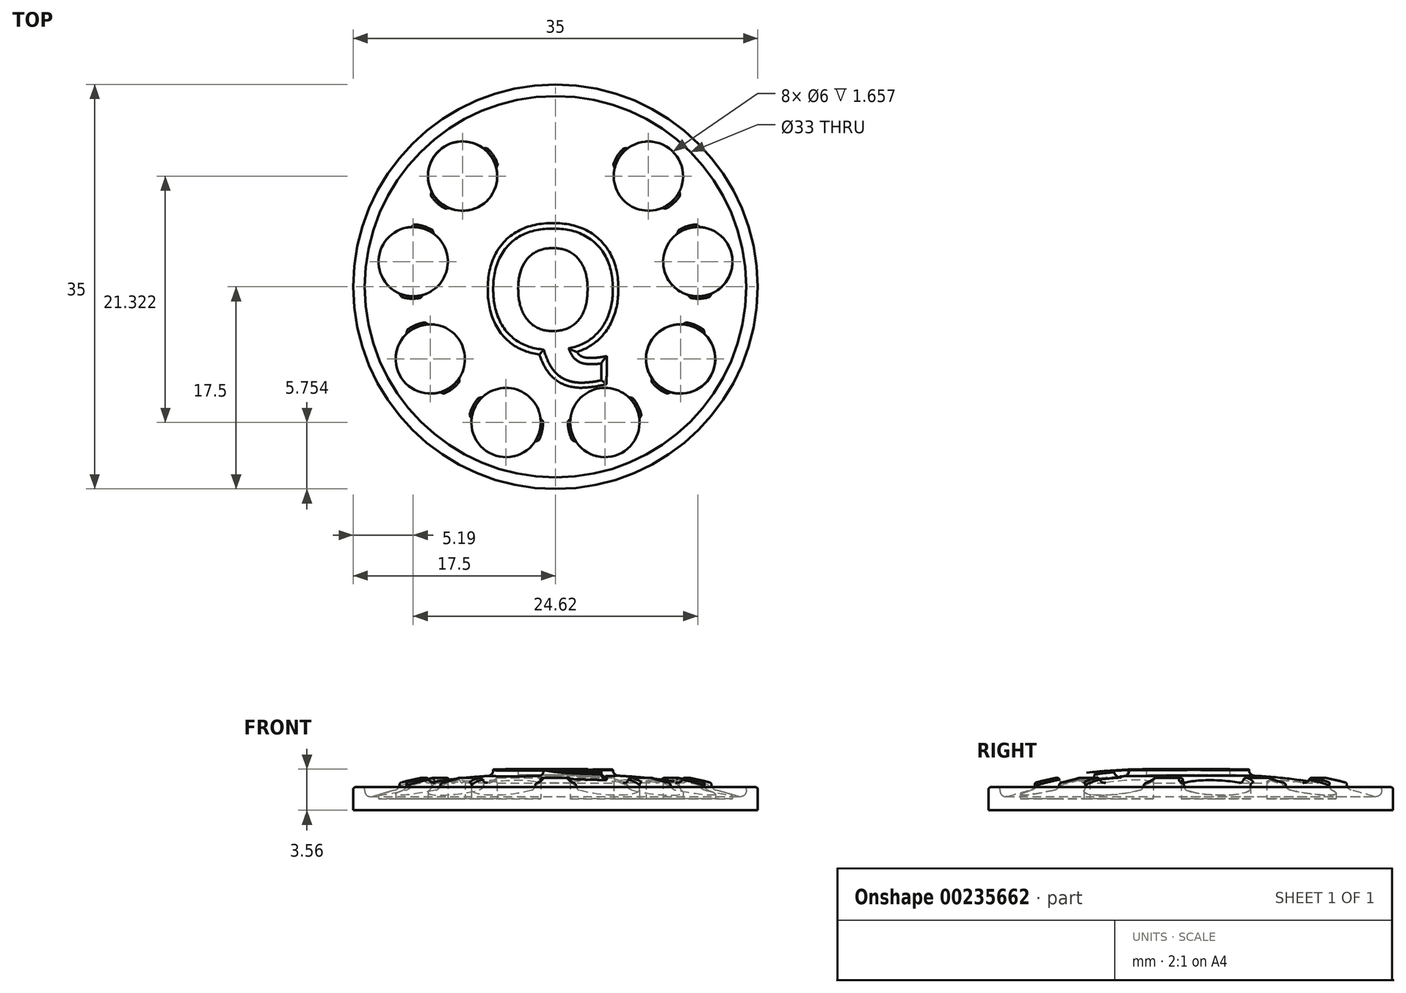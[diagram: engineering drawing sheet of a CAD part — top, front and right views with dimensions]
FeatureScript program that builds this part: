
annotation { "Feature Type Name" : "Feature", "Feature Type Description" : "" }
export const myFeature = defineFeature(function(context is Context, id is Id, definition is map)
    precondition{}
    {
        {
            var Q0;
            Q0=qCreatedBy(makeId("Top.planeOp"),FACE);
            var sketch = newSketch(context, id + "F0", { "sketchPlane" : qUnion([Q0])});
            skCircle(sketch, "E0", {"center": v(0, 0) * mm, "radius": 17.5 * mm});
            skCircle(sketch, "E1", {"center": v(0, 0) * mm, "radius": 16.5 * mm});
            skLineSegment(sketch, "E2", {"start": v(0, 0) * mm, "end": v(0, 16.5) * mm, "construction": true});
            skLineSegment(sketch, "E3", {"start": v(0, 0) * mm, "end": v(0, -16.5) * mm, "construction": true});
            skText(sketch, "E4", { "text": "Q", "fontName": "Arimo-Bold.ttf"});
            skCircle(sketch, "E5", {"center": v(0, 0) * mm, "radius": 12.5 * mm, "construction": true});
            skCircle(sketch, "E6", {"center": v(0, 12.5) * mm, "radius": 3 * mm});
            skCircle(sketch, "E7.1.0", {"center": v(-8.03, 9.58) * mm, "radius": 3 * mm});
            skCircle(sketch, "E7.2.0", {"center": v(-12.31, 2.17) * mm, "radius": 3 * mm});
            skCircle(sketch, "E7.3.0", {"center": v(-10.83, -6.25) * mm, "radius": 3 * mm});
            skCircle(sketch, "E7.4.0", {"center": v(-4.28, -11.75) * mm, "radius": 3 * mm});
            skCircle(sketch, "E7.5.0", {"center": v(4.28, -11.75) * mm, "radius": 3 * mm});
            skCircle(sketch, "E7.6.0", {"center": v(10.83, -6.25) * mm, "radius": 3 * mm});
            skCircle(sketch, "E7.7.0", {"center": v(12.31, 2.17) * mm, "radius": 3 * mm});
            skCircle(sketch, "E8.1.8.0", {"center": v(8.03, 9.58) * mm, "radius": 3 * mm});
            const initialGuessF0  = {"E4": [-0.006, -0.00537, 1, 0, 0.01073]};
            skSetInitialGuess(sketch, initialGuessF0);
            skSolve(sketch);
        }
        {
            var Q0;
            Q0=qCreatedBy(makeId("Front.planeOp"),FACE);
            var sketch = newSketch(context, id + "F1", { "sketchPlane" : qUnion([Q0])});
            skLineSegment(sketch, "E9.0", {"start": v(-16.5, 0) * mm, "end": v(16.5, 0) * mm});
            skLineSegment(sketch, "E10.0", {"start": v(-17.5, 0) * mm, "end": v(17.5, 0) * mm});
            skLineSegment(sketch, "E11", {"start": v(-17.5, 0) * mm, "end": v(-17.5, 1.8) * mm});
            skLineSegment(sketch, "E12", {"start": v(-17.3, 2) * mm, "end": v(-16.7, 2) * mm});
            skLineSegment(sketch, "E13", {"start": v(-16.5, 1.8) * mm, "end": v(-16.5, 1.67) * mm});
            skLineSegment(sketch, "E14", {"start": v(0, 0) * mm, "end": v(0, 3) * mm});
            skFitSpline(sketch, "E15", {"points": [v(-16.5, 1) * mm, v(0, 3) * mm], "startDerivative": vector(10.42, 3.22) * mm, "endDerivative": vector(24.57, -1.03) * mm});
            skArc(sketch, "E16.filletArc", {"start": v(-16.5, 1.67) * mm, "mid": v(-16.3, 1.27) * mm, "end": v(-15.86, 1.2) * mm});
            skPoint(sketch, "E17.visualSharp", {"position": v(-17.5, 2) * mm});
            skArc(sketch, "E17.filletArc", {"start": v(-17.3, 2) * mm, "mid": v(-17.44, 1.94) * mm, "end": v(-17.5, 1.8) * mm});
            skPoint(sketch, "E18.visualSharp", {"position": v(-16.5, 2) * mm});
            skArc(sketch, "E18.filletArc", {"start": v(-16.5, 1.8) * mm, "mid": v(-16.56, 1.94) * mm, "end": v(-16.7, 2) * mm});
            skLineSegment(sketch, "E19", {"start": v(-15.86, 1.2) * mm, "end": v(-15.86, 2.88) * mm, "construction": true});
            skLineSegment(sketch, "E20", {"start": v(0, 3) * mm, "end": v(0, 5.02) * mm, "construction": true});
            skPoint(sketch, "E21", {"position": v(0, 3.5) * mm});
            skPoint(sketch, "E22", {"position": v(-15.86, 1.7) * mm});
            skFitSpline(sketch, "E23", {"points": [v(-15.86, 1.7) * mm, v(0, 3.5) * mm], "startDerivative": vector(11.8, 3.63) * mm, "endDerivative": vector(24.86, -0.94) * mm});
            skLineSegment(sketch, "E24", {"start": v(-15.86, 1.7) * mm, "end": v(-15.86, 7.13) * mm});
            skPoint(sketch, "E24.endSnap0", {"position": v(-15.86, 2.04) * mm});
            skLineSegment(sketch, "E25", {"start": v(0, 3.5) * mm, "end": v(0, 7.13) * mm});
            skLineSegment(sketch, "E26", {"start": v(0, 7.13) * mm, "end": v(-15.86, 7.13) * mm});
            skSolve(sketch);
        }
        {
            var Q0;
            Q0=qCreatedBy(makeId("Top.planeOp"),FACE);
            cPlane(context, id + "F2", {"entities" : qUnion([Q0]), "cplaneType" : CPlaneType.OFFSET, "offset" : 1 * mm, "width" : 150 * mm, "height" : 150 * mm});
        }
        {
            var Q0;
            Q0=qCreatedBy(id+"F2.planeOp",FACE);
            var sketch = newSketch(context, id + "F3", { "sketchPlane" : qUnion([Q0])});
            skCircle(sketch, "E27.1", {"center": v(12.31, 2.17) * mm, "radius": 3 * mm});
            skCircle(sketch, "E27.2", {"center": v(10.83, -6.25) * mm, "radius": 3 * mm});
            skCircle(sketch, "E27.3", {"center": v(4.28, -11.75) * mm, "radius": 3 * mm});
            skCircle(sketch, "E27.4", {"center": v(-4.28, -11.75) * mm, "radius": 3 * mm});
            skCircle(sketch, "E27.5", {"center": v(-10.83, -6.25) * mm, "radius": 3 * mm});
            skCircle(sketch, "E27.6", {"center": v(-12.31, 2.17) * mm, "radius": 3 * mm});
            skCircle(sketch, "E27.7", {"center": v(-8.03, 9.58) * mm, "radius": 3 * mm});
            skCircle(sketch, "E28.0", {"center": v(8.03, 9.58) * mm, "radius": 3 * mm});
            skCircle(sketch, "E29.0", {"center": v(0, 0) * mm, "radius": 12.5 * mm, "construction": true});
            skArc(sketch, "E30", {"start": v(-10.71, 8.22) * mm, "mid": v(-11.7, 6.75) * mm, "end": v(-12.47, 5.17) * mm});
            skArc(sketch, "E31", {"start": v(-9.25, 6.83) * mm, "mid": v(-9.96, 5.75) * mm, "end": v(-10.54, 4.6) * mm});
            skArc(sketch, "E32.0", {"start": v(-2.92, 13.18) * mm, "mid": v(-2.98, 12.16) * mm, "end": v(-2.7, 11.18) * mm});
            skArc(sketch, "E33.trimOffspring", {"start": v(-13.49, -0.59) * mm, "mid": v(-13.3, -2.34) * mm, "end": v(-12.88, -4.06) * mm});
            skArc(sketch, "E34.trimOffspring", {"start": v(-11.48, -0.71) * mm, "mid": v(-11.33, -2) * mm, "end": v(-11.03, -3.26) * mm});
            skArc(sketch, "E35.trimOffspring", {"start": v(-9.95, -9.12) * mm, "mid": v(-8.68, -10.34) * mm, "end": v(-7.25, -11.39) * mm});
            skArc(sketch, "E36.trimOffspring", {"start": v(-8.34, -7.92) * mm, "mid": v(-7.4, -8.8) * mm, "end": v(-6.36, -9.58) * mm});
            skArc(sketch, "E37.trimOffspring", {"start": v(-1.3, -11.43) * mm, "mid": v(0, -11.5) * mm, "end": v(1.3, -11.43) * mm});
            skArc(sketch, "E38.trimOffspring", {"start": v(-1.76, -13.38) * mm, "mid": v(0, -13.5) * mm, "end": v(1.76, -13.38) * mm});
            skArc(sketch, "E39.trimOffspring", {"start": v(6.36, -9.58) * mm, "mid": v(7.4, -8.8) * mm, "end": v(8.34, -7.92) * mm});
            skArc(sketch, "E40.trimOffspring", {"start": v(7.25, -11.39) * mm, "mid": v(8.68, -10.34) * mm, "end": v(9.95, -9.12) * mm});
            skArc(sketch, "E41.trimOffspring", {"start": v(11.03, -3.26) * mm, "mid": v(11.33, -2) * mm, "end": v(11.48, -0.71) * mm});
            skArc(sketch, "E42.trimOffspring", {"start": v(12.88, -4.06) * mm, "mid": v(13.3, -2.34) * mm, "end": v(13.49, -0.59) * mm});
            skArc(sketch, "E43.trimOffspring", {"start": v(10.54, 4.6) * mm, "mid": v(9.96, 5.75) * mm, "end": v(9.25, 6.83) * mm});
            skArc(sketch, "E44.trimOffspring", {"start": v(12.47, 5.17) * mm, "mid": v(11.7, 6.75) * mm, "end": v(10.71, 8.22) * mm});
            skArc(sketch, "E45.trimOffspring", {"start": v(5.12, 10.3) * mm, "mid": v(0, 11.5) * mm, "end": v(-5.12, 10.3) * mm});
            skArc(sketch, "E46.trimOffspring", {"start": v(6.23, 11.97) * mm, "mid": v(0, 13.5) * mm, "end": v(-6.23, 11.97) * mm});
            skArc(sketch, "E47.trimOffspring", {"start": v(2.7, 11.18) * mm, "mid": v(2.98, 12.16) * mm, "end": v(2.92, 13.18) * mm});
            skSolve(sketch);
        }
        {
            var Q0;
            {var subQ0=sQuery(id+"F1.wireOp",EDGE,"E11");Q0=makeQuery(id+"F1.imprint","IMPRINT",FACE,{"disambiguationData":[TD([[makeQuery(id+"F1.imprint","IMPRINT",EDGE,{"derivedFrom":subQ0}),-1.0]])]});}
            var Q1;
            Q1=sQuery(id+"F1.wireOp",EDGE,"E14");
            revolve(context, id + "F4", {"entities" : qUnion([Q0]), "axis" : qUnion([Q1]), "revolveType" : RevolveType.FULL});
        }
        {
            var Q0;
            {var subQ0=sQuery(id+"F3.wireOp",EDGE,"E30");Q0=makeQuery(id+"F3.imprint","IMPRINT",FACE,{"disambiguationData":[TD([[makeQuery(id+"F3.imprint","IMPRINT",EDGE,{"derivedFrom":subQ0}),1.0]])]});}
            var Q1;
            {var subQ0=sQuery(id+"F3.wireOp",EDGE,"E33.trimOffspring");Q1=makeQuery(id+"F3.imprint","IMPRINT",FACE,{"disambiguationData":[TD([[makeQuery(id+"F3.imprint","IMPRINT",EDGE,{"derivedFrom":subQ0}),1.0]])]});}
            var Q2;
            {var subQ0=sQuery(id+"F3.wireOp",EDGE,"E35.trimOffspring");Q2=makeQuery(id+"F3.imprint","IMPRINT",FACE,{"disambiguationData":[TD([[makeQuery(id+"F3.imprint","IMPRINT",EDGE,{"derivedFrom":subQ0}),1.0]])]});}
            var Q3;
            {var subQ0=sQuery(id+"F3.wireOp",EDGE,"E37.trimOffspring");Q3=makeQuery(id+"F3.imprint","IMPRINT",FACE,{"disambiguationData":[TD([[makeQuery(id+"F3.imprint","IMPRINT",EDGE,{"derivedFrom":subQ0}),-1.0]])]});}
            var Q4;
            {var subQ0=sQuery(id+"F3.wireOp",EDGE,"E39.trimOffspring");Q4=makeQuery(id+"F3.imprint","IMPRINT",FACE,{"disambiguationData":[TD([[makeQuery(id+"F3.imprint","IMPRINT",EDGE,{"derivedFrom":subQ0}),-1.0]])]});}
            var Q5;
            {var subQ0=sQuery(id+"F3.wireOp",EDGE,"E41.trimOffspring");Q5=makeQuery(id+"F3.imprint","IMPRINT",FACE,{"disambiguationData":[TD([[makeQuery(id+"F3.imprint","IMPRINT",EDGE,{"derivedFrom":subQ0}),-1.0]])]});}
            var Q6;
            {var subQ0=sQuery(id+"F3.wireOp",EDGE,"E43.trimOffspring");Q6=makeQuery(id+"F3.imprint","IMPRINT",FACE,{"disambiguationData":[TD([[makeQuery(id+"F3.imprint","IMPRINT",EDGE,{"derivedFrom":subQ0}),-1.0]])]});}
            var Q7;
            {var subQ5=sQuery(id+"F3.wireOp",EDGE,"E47.trimOffspring");Q7=makeQuery(id+"F3.imprint","IMPRINT",FACE,{"disambiguationData":[TD([[makeQuery(id+"F3.imprint","IMPRINT",EDGE,{"derivedFrom":subQ5}),-1.0]])]});}
            var Q8;
            {var subQ0=sQuery(id+"F3.wireOp",EDGE,"E32.0");Q8=makeQuery(id+"F3.imprint","IMPRINT",FACE,{"disambiguationData":[TD([[makeQuery(id+"F3.imprint","IMPRINT",EDGE,{"derivedFrom":subQ0}),1.0]])]});}
            var Q9;
            {var subQ5=sQuery(id+"F3.wireOp",EDGE,"E32.0");Q9=makeQuery(id+"F3.imprint","IMPRINT",FACE,{"disambiguationData":[TD([[makeQuery(id+"F3.imprint","IMPRINT",EDGE,{"derivedFrom":subQ5}),-1.0]])]});}
            extrude(context, id + "F5", {"entities" : qUnion([Q0, Q1, Q2, Q3, Q4, Q5, Q6, Q7, Q8, Q9]), "operationType" : NewBodyOperationType.ADD, "depth" : 5 * mm});
        }
        {
            var Q0;
            Q0=makeQuery(id+"F0.imprint","IMPRINT",FACE,{"disambiguationData":[TD([[makeQuery(id+"F0.imprint","IMPRINT",EDGE,{"derivedFrom":sQuery(id+"F0.wireOp",EDGE,"E4.sketch_text.stroke-0")}),-1.0]])]});
            extrude(context, id + "F6", {"entities" : qUnion([Q0]), "operationType" : NewBodyOperationType.ADD, "depth" : 5 * mm});
        }
        {
            var Q0;
            Q0=makeQuery(id+"F1.imprint","IMPRINT",FACE,{"disambiguationData":[TD([[makeQuery(id+"F1.imprint","IMPRINT",EDGE,{"derivedFrom":sQuery(id+"F1.wireOp",EDGE,"E23")}),1.0]])]});
            var Q1;
            Q1=sQuery(id+"F1.wireOp",EDGE,"E25");
            revolve(context, id + "F7", {"operationType" : NewBodyOperationType.REMOVE, "entities" : qUnion([Q0]), "axis" : qUnion([Q1]), "revolveType" : RevolveType.FULL, "oppositeDirection" : true});
        }
        {
            var Q0;
            Q0=makeQuery(id+"F3.imprint","IMPRINT",FACE,{"disambiguationData":[TD([[makeQuery(id+"F3.imprint","IMPRINT",EDGE,{"derivedFrom":sQuery(id+"F3.wireOp",EDGE,"E27.7")}),1.0]])]});
            var Q1;
            Q1=makeQuery(id+"F3.imprint","IMPRINT",FACE,{"disambiguationData":[TD([[makeQuery(id+"F3.imprint","IMPRINT",EDGE,{"derivedFrom":sQuery(id+"F3.wireOp",EDGE,"E27.6")}),1.0]])]});
            var Q2;
            Q2=makeQuery(id+"F3.imprint","IMPRINT",FACE,{"disambiguationData":[TD([[makeQuery(id+"F3.imprint","IMPRINT",EDGE,{"derivedFrom":sQuery(id+"F3.wireOp",EDGE,"E27.5")}),1.0]])]});
            var Q3;
            Q3=makeQuery(id+"F3.imprint","IMPRINT",FACE,{"disambiguationData":[TD([[makeQuery(id+"F3.imprint","IMPRINT",EDGE,{"derivedFrom":sQuery(id+"F3.wireOp",EDGE,"E27.4")}),1.0]])]});
            var Q4;
            Q4=makeQuery(id+"F3.imprint","IMPRINT",FACE,{"disambiguationData":[TD([[makeQuery(id+"F3.imprint","IMPRINT",EDGE,{"derivedFrom":sQuery(id+"F3.wireOp",EDGE,"E27.3")}),1.0]])]});
            var Q5;
            Q5=makeQuery(id+"F3.imprint","IMPRINT",FACE,{"disambiguationData":[TD([[makeQuery(id+"F3.imprint","IMPRINT",EDGE,{"derivedFrom":sQuery(id+"F3.wireOp",EDGE,"E27.2")}),1.0]])]});
            var Q6;
            Q6=makeQuery(id+"F3.imprint","IMPRINT",FACE,{"disambiguationData":[TD([[makeQuery(id+"F3.imprint","IMPRINT",EDGE,{"derivedFrom":sQuery(id+"F3.wireOp",EDGE,"E27.1")}),1.0]])]});
            var Q7;
            Q7=makeQuery(id+"F3.imprint","IMPRINT",FACE,{"disambiguationData":[TD([[makeQuery(id+"F3.imprint","IMPRINT",EDGE,{"derivedFrom":sQuery(id+"F3.wireOp",EDGE,"E28.0")}),1.0]])]});
            extrude(context, id + "F8", {"entities" : qUnion([Q0, Q1, Q2, Q3, Q4, Q5, Q6, Q7]), "operationType" : NewBodyOperationType.REMOVE, "depth" : 25 * mm});
        }
        {
            var Q0;
            Q0=makeQuery(id+"F5.boolean.opBoolean","INTERSECT",EDGE,{"derivedFrom":[makeQuery(id+"F4.opRevolve","SWEPT_FACE",FACE,{"disambiguationData":[OSD([sQuery(id+"F1.wireOp",EDGE,"E15")])]}),makeQuery(id+"F5.opExtrude","SWEPT_FACE",FACE,{"disambiguationData":[OSD([sQuery(id+"F3.wireOp",EDGE,"E31")])]})]});
            var Q1;
            Q1=makeQuery(id+"F5.boolean.opBoolean","INTERSECT",EDGE,{"derivedFrom":[makeQuery(id+"F4.opRevolve","SWEPT_FACE",FACE,{"disambiguationData":[OSD([sQuery(id+"F1.wireOp",EDGE,"E15")])]}),makeQuery(id+"F5.opExtrude","SWEPT_FACE",FACE,{"disambiguationData":[OSD([sQuery(id+"F3.wireOp",EDGE,"E45.trimOffspring")])]})]});
            var Q2;
            Q2=makeQuery(id+"F5.boolean.opBoolean","INTERSECT",EDGE,{"derivedFrom":[makeQuery(id+"F4.opRevolve","SWEPT_FACE",FACE,{"disambiguationData":[OSD([sQuery(id+"F1.wireOp",EDGE,"E15")])]}),makeQuery(id+"F5.opExtrude","SWEPT_FACE",FACE,{"disambiguationData":[OSD([sQuery(id+"F3.wireOp",EDGE,"E43.trimOffspring")])]})]});
            var Q3;
            Q3=makeQuery(id+"F5.boolean.opBoolean","INTERSECT",EDGE,{"derivedFrom":[makeQuery(id+"F4.opRevolve","SWEPT_FACE",FACE,{"disambiguationData":[OSD([sQuery(id+"F1.wireOp",EDGE,"E15")])]}),makeQuery(id+"F5.opExtrude","SWEPT_FACE",FACE,{"disambiguationData":[OSD([sQuery(id+"F3.wireOp",EDGE,"E41.trimOffspring")])]})]});
            var Q4;
            Q4=makeQuery(id+"F5.boolean.opBoolean","INTERSECT",EDGE,{"derivedFrom":[makeQuery(id+"F4.opRevolve","SWEPT_FACE",FACE,{"disambiguationData":[OSD([sQuery(id+"F1.wireOp",EDGE,"E15")])]}),makeQuery(id+"F5.opExtrude","SWEPT_FACE",FACE,{"disambiguationData":[OSD([sQuery(id+"F3.wireOp",EDGE,"E39.trimOffspring")])]})]});
            var Q5;
            Q5=makeQuery(id+"F5.boolean.opBoolean","INTERSECT",EDGE,{"derivedFrom":[makeQuery(id+"F4.opRevolve","SWEPT_FACE",FACE,{"disambiguationData":[OSD([sQuery(id+"F1.wireOp",EDGE,"E15")])]}),makeQuery(id+"F5.opExtrude","SWEPT_FACE",FACE,{"disambiguationData":[OSD([sQuery(id+"F3.wireOp",EDGE,"E34.trimOffspring")])]})]});
            var Q6;
            Q6=makeQuery(id+"F5.boolean.opBoolean","INTERSECT",EDGE,{"derivedFrom":[makeQuery(id+"F4.opRevolve","SWEPT_FACE",FACE,{"disambiguationData":[OSD([sQuery(id+"F1.wireOp",EDGE,"E15")])]}),makeQuery(id+"F5.opExtrude","SWEPT_FACE",FACE,{"disambiguationData":[OSD([sQuery(id+"F3.wireOp",EDGE,"E36.trimOffspring")])]})]});
            var Q7;
            Q7=makeQuery(id+"F5.boolean.opBoolean","INTERSECT",EDGE,{"derivedFrom":[makeQuery(id+"F4.opRevolve","SWEPT_FACE",FACE,{"disambiguationData":[OSD([sQuery(id+"F1.wireOp",EDGE,"E15")])]}),makeQuery(id+"F5.opExtrude","SWEPT_FACE",FACE,{"disambiguationData":[OSD([sQuery(id+"F3.wireOp",EDGE,"E37.trimOffspring")])]})]});
            var Q8;
            Q8=makeQuery(id+"F5.boolean.opBoolean","INTERSECT",EDGE,{"derivedFrom":[makeQuery(id+"F4.opRevolve","SWEPT_FACE",FACE,{"disambiguationData":[OSD([sQuery(id+"F1.wireOp",EDGE,"E15")])]}),makeQuery(id+"F5.opExtrude","SWEPT_FACE",FACE,{"disambiguationData":[OSD([sQuery(id+"F3.wireOp",EDGE,"E38.trimOffspring")])]})]});
            var Q9;
            Q9=makeQuery(id+"F5.boolean.opBoolean","INTERSECT",EDGE,{"derivedFrom":[makeQuery(id+"F4.opRevolve","SWEPT_FACE",FACE,{"disambiguationData":[OSD([sQuery(id+"F1.wireOp",EDGE,"E15")])]}),makeQuery(id+"F5.opExtrude","SWEPT_FACE",FACE,{"disambiguationData":[OSD([sQuery(id+"F3.wireOp",EDGE,"E40.trimOffspring")])]})]});
            var Q10;
            Q10=makeQuery(id+"F5.boolean.opBoolean","INTERSECT",EDGE,{"derivedFrom":[makeQuery(id+"F4.opRevolve","SWEPT_FACE",FACE,{"disambiguationData":[OSD([sQuery(id+"F1.wireOp",EDGE,"E15")])]}),makeQuery(id+"F5.opExtrude","SWEPT_FACE",FACE,{"disambiguationData":[OSD([sQuery(id+"F3.wireOp",EDGE,"E35.trimOffspring")])]})]});
            var Q11;
            Q11=makeQuery(id+"F5.boolean.opBoolean","INTERSECT",EDGE,{"derivedFrom":[makeQuery(id+"F4.opRevolve","SWEPT_FACE",FACE,{"disambiguationData":[OSD([sQuery(id+"F1.wireOp",EDGE,"E15")])]}),makeQuery(id+"F5.opExtrude","SWEPT_FACE",FACE,{"disambiguationData":[OSD([sQuery(id+"F3.wireOp",EDGE,"E33.trimOffspring")])]})]});
            var Q12;
            Q12=makeQuery(id+"F5.boolean.opBoolean","INTERSECT",EDGE,{"derivedFrom":[makeQuery(id+"F4.opRevolve","SWEPT_FACE",FACE,{"disambiguationData":[OSD([sQuery(id+"F1.wireOp",EDGE,"E15")])]}),makeQuery(id+"F5.opExtrude","SWEPT_FACE",FACE,{"disambiguationData":[OSD([sQuery(id+"F3.wireOp",EDGE,"E30")])]})]});
            var Q13;
            Q13=makeQuery(id+"F5.boolean.opBoolean","INTERSECT",EDGE,{"derivedFrom":[makeQuery(id+"F4.opRevolve","SWEPT_FACE",FACE,{"disambiguationData":[OSD([sQuery(id+"F1.wireOp",EDGE,"E15")])]}),makeQuery(id+"F5.opExtrude","SWEPT_FACE",FACE,{"disambiguationData":[OSD([sQuery(id+"F3.wireOp",EDGE,"E42.trimOffspring")])]})]});
            var Q14;
            Q14=makeQuery(id+"F5.boolean.opBoolean","INTERSECT",EDGE,{"derivedFrom":[makeQuery(id+"F4.opRevolve","SWEPT_FACE",FACE,{"disambiguationData":[OSD([sQuery(id+"F1.wireOp",EDGE,"E15")])]}),makeQuery(id+"F5.opExtrude","SWEPT_FACE",FACE,{"disambiguationData":[OSD([sQuery(id+"F3.wireOp",EDGE,"E44.trimOffspring")])]})]});
            var Q15;
            Q15=makeQuery(id+"F5.boolean.opBoolean","INTERSECT",EDGE,{"derivedFrom":[makeQuery(id+"F4.opRevolve","SWEPT_FACE",FACE,{"disambiguationData":[OSD([sQuery(id+"F1.wireOp",EDGE,"E15")])]}),makeQuery(id+"F5.opExtrude","SWEPT_FACE",FACE,{"disambiguationData":[OSD([sQuery(id+"F3.wireOp",EDGE,"E46.trimOffspring")])]})]});
            var Q16;
            Q16=makeQuery(id+"F6.boolean.opBoolean","INTERSECT",EDGE,{"derivedFrom":[makeQuery(id+"F4.opRevolve","SWEPT_FACE",FACE,{"disambiguationData":[OSD([sQuery(id+"F1.wireOp",EDGE,"E15")])]}),makeQuery(id+"F6.opExtrude","SWEPT_FACE",FACE,{"disambiguationData":[OSD([sQuery(id+"F0.wireOp",EDGE,"E4.sketch_text.stroke-9")])]})]});
            var Q17;
            Q17=makeQuery(id+"F6.boolean.opBoolean","INTERSECT",EDGE,{"derivedFrom":[makeQuery(id+"F4.opRevolve","SWEPT_FACE",FACE,{"disambiguationData":[OSD([sQuery(id+"F1.wireOp",EDGE,"E15")])]}),makeQuery(id+"F6.opExtrude","SWEPT_FACE",FACE,{"disambiguationData":[OSD([sQuery(id+"F0.wireOp",EDGE,"E4.sketch_text.stroke-7")])]})]});
            var Q18;
            Q18=makeQuery(id+"F6.boolean.opBoolean","INTERSECT",EDGE,{"derivedFrom":[makeQuery(id+"F4.opRevolve","SWEPT_FACE",FACE,{"disambiguationData":[OSD([sQuery(id+"F1.wireOp",EDGE,"E15")])]}),makeQuery(id+"F6.opExtrude","SWEPT_FACE",FACE,{"disambiguationData":[OSD([sQuery(id+"F0.wireOp",EDGE,"E4.sketch_text.stroke-5")])]})]});
            var Q19;
            Q19=makeQuery(id+"F6.boolean.opBoolean","INTERSECT",EDGE,{"derivedFrom":[makeQuery(id+"F4.opRevolve","SWEPT_FACE",FACE,{"disambiguationData":[OSD([sQuery(id+"F1.wireOp",EDGE,"E15")])]}),makeQuery(id+"F6.opExtrude","SWEPT_FACE",FACE,{"disambiguationData":[OSD([sQuery(id+"F0.wireOp",EDGE,"E4.sketch_text.stroke-3")])]})]});
            fillet(context, id + "F9", {"entities" : qUnion([Q0, Q1, Q2, Q3, Q4, Q5, Q6, Q7, Q8, Q9, Q10, Q11, Q12, Q13, Q14, Q15, Q16, Q17, Q18, Q19]), "radius" : .5 * mm, "tangentPropagation" : true, "allowEdgeOverflow" : false});
        }
        {
            var Q0;
            {var subQ0=sQuery(id+"F3.wireOp",EDGE,"E37.trimOffspring");Q0=makeQuery(id+"F7.boolean.opBoolean","COPY",FACE,{"disambiguationData":[TD([makeQuery(id+"F5.opExtrude","SWEPT_FACE",FACE,{"disambiguationData":[OSD([subQ0])]})])],"derivedFrom":makeQuery(id+"F7.opRevolve","SWEPT_FACE",FACE,{"disambiguationData":[OSD([sQuery(id+"F1.wireOp",EDGE,"E23")])]})});}
            var Q1;
            {var subQ0=sQuery(id+"F3.wireOp",EDGE,"E39.trimOffspring");Q1=makeQuery(id+"F7.boolean.opBoolean","COPY",FACE,{"disambiguationData":[TD([makeQuery(id+"F5.opExtrude","SWEPT_FACE",FACE,{"disambiguationData":[OSD([subQ0])]})])],"derivedFrom":makeQuery(id+"F7.opRevolve","SWEPT_FACE",FACE,{"disambiguationData":[OSD([sQuery(id+"F1.wireOp",EDGE,"E23")])]})});}
            var Q2;
            {var subQ0=sQuery(id+"F3.wireOp",EDGE,"E41.trimOffspring");Q2=makeQuery(id+"F7.boolean.opBoolean","COPY",FACE,{"disambiguationData":[TD([makeQuery(id+"F5.opExtrude","SWEPT_FACE",FACE,{"disambiguationData":[OSD([subQ0])]})])],"derivedFrom":makeQuery(id+"F7.opRevolve","SWEPT_FACE",FACE,{"disambiguationData":[OSD([sQuery(id+"F1.wireOp",EDGE,"E23")])]})});}
            var Q3;
            {var subQ0=sQuery(id+"F3.wireOp",EDGE,"E43.trimOffspring");Q3=makeQuery(id+"F7.boolean.opBoolean","COPY",FACE,{"disambiguationData":[TD([makeQuery(id+"F5.opExtrude","SWEPT_FACE",FACE,{"disambiguationData":[OSD([subQ0])]})])],"derivedFrom":makeQuery(id+"F7.opRevolve","SWEPT_FACE",FACE,{"disambiguationData":[OSD([sQuery(id+"F1.wireOp",EDGE,"E23")])]})});}
            var Q4;
            {var subQ0=sQuery(id+"F3.wireOp",EDGE,"E45.trimOffspring");Q4=makeQuery(id+"F7.boolean.opBoolean","COPY",FACE,{"disambiguationData":[TD([makeQuery(id+"F5.opExtrude","SWEPT_FACE",FACE,{"disambiguationData":[OSD([subQ0])]})])],"derivedFrom":makeQuery(id+"F7.opRevolve","SWEPT_FACE",FACE,{"disambiguationData":[OSD([sQuery(id+"F1.wireOp",EDGE,"E23")])]})});}
            var Q5;
            {var subQ0=sQuery(id+"F3.wireOp",EDGE,"E30");Q5=makeQuery(id+"F7.boolean.opBoolean","COPY",FACE,{"disambiguationData":[TD([makeQuery(id+"F5.opExtrude","SWEPT_FACE",FACE,{"disambiguationData":[OSD([subQ0])]})])],"derivedFrom":makeQuery(id+"F7.opRevolve","SWEPT_FACE",FACE,{"disambiguationData":[OSD([sQuery(id+"F1.wireOp",EDGE,"E23")])]})});}
            var Q6;
            {var subQ0=sQuery(id+"F3.wireOp",EDGE,"E33.trimOffspring");Q6=makeQuery(id+"F7.boolean.opBoolean","COPY",FACE,{"disambiguationData":[TD([makeQuery(id+"F5.opExtrude","SWEPT_FACE",FACE,{"disambiguationData":[OSD([subQ0])]})])],"derivedFrom":makeQuery(id+"F7.opRevolve","SWEPT_FACE",FACE,{"disambiguationData":[OSD([sQuery(id+"F1.wireOp",EDGE,"E23")])]})});}
            var Q7;
            {var subQ0=sQuery(id+"F3.wireOp",EDGE,"E35.trimOffspring");Q7=makeQuery(id+"F7.boolean.opBoolean","COPY",FACE,{"disambiguationData":[TD([makeQuery(id+"F5.opExtrude","SWEPT_FACE",FACE,{"disambiguationData":[OSD([subQ0])]})])],"derivedFrom":makeQuery(id+"F7.opRevolve","SWEPT_FACE",FACE,{"disambiguationData":[OSD([sQuery(id+"F1.wireOp",EDGE,"E23")])]})});}
            fillet(context, id + "F10", {"entities" : qUnion([Q0, Q1, Q2, Q3, Q4, Q5, Q6, Q7]), "radius" : .2 * mm, "tangentPropagation" : true, "allowEdgeOverflow" : false});
        }
    });
